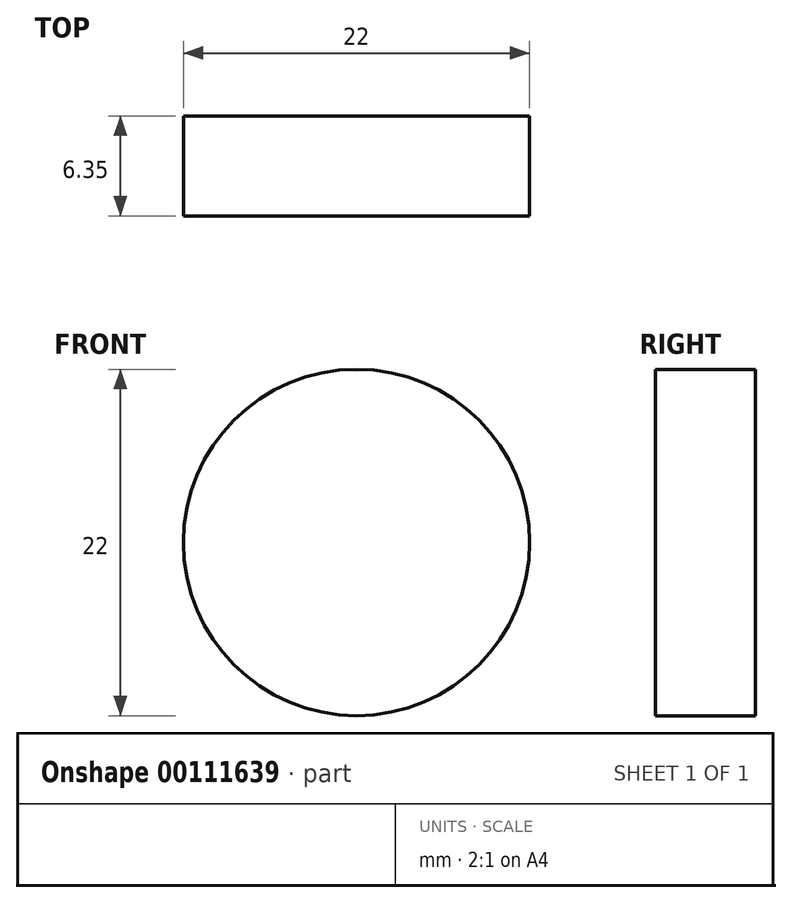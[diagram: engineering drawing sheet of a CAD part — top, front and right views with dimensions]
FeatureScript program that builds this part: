
annotation { "Feature Type Name" : "Feature", "Feature Type Description" : "" }
export const myFeature = defineFeature(function(context is Context, id is Id, definition is map)
    precondition{}
    {
        {
            var Q0;
            Q0=qCreatedBy(makeId("Front.planeOp"),FACE);
            var sketch = newSketch(context, id + "F0", { "sketchPlane" : qUnion([Q0])});
            skCircle(sketch, "E0", {"center": v(0, 0) * mm, "radius": 11 * mm});
            skLineSegment(sketch, "E1", {"start": v(-11, 0) * mm, "end": v(11, 0) * mm});
            skSolve(sketch);
        }
        {
            var Q0;
            Q0 = qSketchRegion(id + "F0", true);
            extrude(context, id + "F1", {"entities" : qUnion([Q0]), "depth" : 6.35 * mm});
        }
    });
